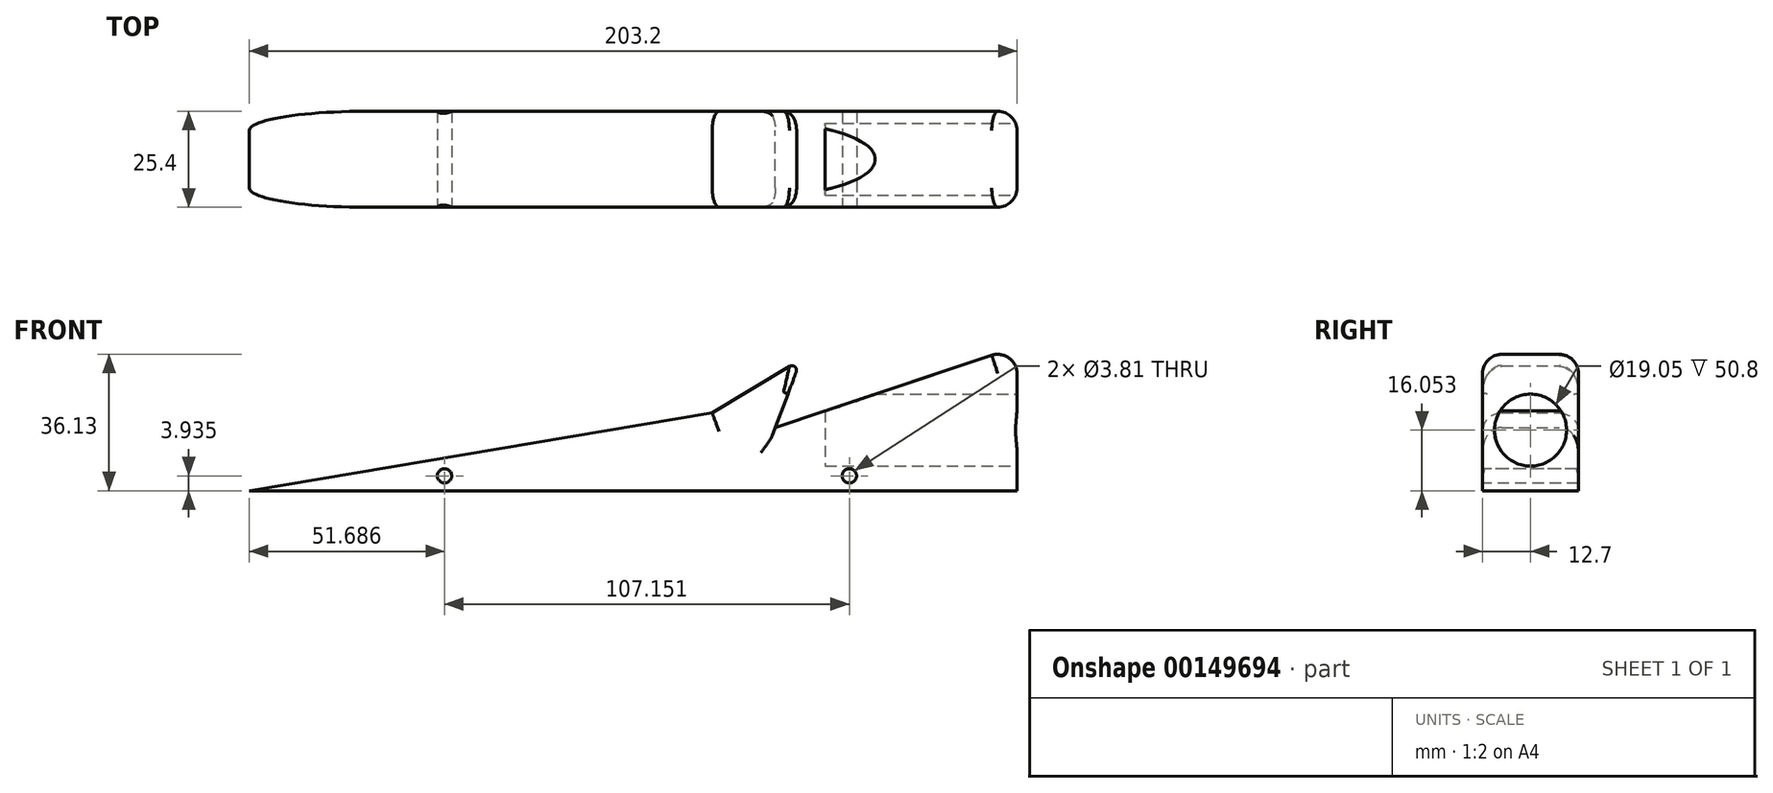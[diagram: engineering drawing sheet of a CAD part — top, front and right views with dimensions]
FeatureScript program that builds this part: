
annotation { "Feature Type Name" : "Feature", "Feature Type Description" : "" }
export const myFeature = defineFeature(function(context is Context, id is Id, definition is map)
    precondition{}
    {
        {
            var Q0;
            Q0=qCreatedBy(makeId("Front.planeOp"),FACE);
            var sketch = newSketch(context, id + "F0", { "sketchPlane" : qUnion([Q0])});
            skLineSegment(sketch, "E0", {"start": v(-98.76, 0) * mm, "end": v(104.44, 0) * mm});
            skLineSegment(sketch, "E1", {"start": v(104.44, 0) * mm, "end": v(104.44, 38.1) * mm});
            skLineSegment(sketch, "E2", {"start": v(-98.76, 0) * mm, "end": v(23.78, 20.59) * mm});
            skLineSegment(sketch, "E3", {"start": v(23.78, 20.59) * mm, "end": v(47.26, 34.81) * mm});
            skLineSegment(sketch, "E4", {"start": v(47.26, 34.81) * mm, "end": v(40.49, 16.75) * mm});
            skLineSegment(sketch, "E5", {"start": v(40.49, 16.75) * mm, "end": v(104.44, 38.1) * mm});
            skSolve(sketch);
        }
        {
            var Q0;
            Q0 = qSketchRegion(id + "F0", true);
            extrude(context, id + "F1", {"entities" : qUnion([Q0]), "depth" : 25.4 * mm});
        }
        {
            var Q0;
            Q0=makeQuery(id+"F1.opExtrude","SWEPT_FACE",FACE,{"disambiguationData":[OSD([sQuery(id+"F0.wireOp",EDGE,"E1")])]});
            var sketch = newSketch(context, id + "F2", { "sketchPlane" : qUnion([Q0])});
            skCircle(sketch, "E6", {"center": v(-12.7, 16.05) * mm, "radius": 9.53 * mm});
            skSolve(sketch);
        }
        {
            var Q0;
            Q0=makeQuery(id+"F1.opExtrude","CAP_FACE",FACE,{"disambiguationData":[OSD([sQuery(id+"F0.wireOp",EDGE,"E0"),sQuery(id+"F0.wireOp",EDGE,"E1"),sQuery(id+"F0.wireOp",EDGE,"E2"),sQuery(id+"F0.wireOp",EDGE,"E3"),sQuery(id+"F0.wireOp",EDGE,"E4"),sQuery(id+"F0.wireOp",EDGE,"E5")])],"isStart":false});
            var sketch = newSketch(context, id + "F3", { "sketchPlane" : qUnion([Q0])});
            skCircle(sketch, "E7", {"center": v(-47.07, 3.93) * mm, "radius": 1.9 * mm});
            skCircle(sketch, "E8", {"center": v(60.08, 3.93) * mm, "radius": 1.9 * mm});
            skSolve(sketch);
        }
        {
            var Q0;
            Q0 = qSketchRegion(id + "F3", true);
            extrude(context, id + "F4", {"entities" : qUnion([Q0]), "operationType" : NewBodyOperationType.REMOVE, "oppositeDirection" : true, "depth" : 25.4 * mm});
        }
        {
            var Q0;
            Q0 = qSketchRegion(id + "F2", true);
            extrude(context, id + "F5", {"entities" : qUnion([Q0]), "operationType" : NewBodyOperationType.REMOVE, "oppositeDirection" : true, "depth" : 50.8 * mm});
        }
        {
            var Q0;
            Q0=makeQuery(id+"F1.opExtrude","CAP_EDGE",EDGE,{"disambiguationData":[OSD([sQuery(id+"F0.wireOp",EDGE,"E2")])],"isStart":false});
            var Q1;
            Q1=makeQuery(id+"F1.opExtrude","CAP_EDGE",EDGE,{"disambiguationData":[OSD([sQuery(id+"F0.wireOp",EDGE,"E2")])],"isStart":true});
            var Q2;
            Q2=makeQuery(id+"F1.opExtrude","CAP_EDGE",EDGE,{"disambiguationData":[OSD([sQuery(id+"F0.wireOp",EDGE,"E3")])],"isStart":true});
            var Q3;
            Q3=makeQuery(id+"F1.opExtrude","CAP_EDGE",EDGE,{"disambiguationData":[OSD([sQuery(id+"F0.wireOp",EDGE,"E3")])],"isStart":false});
            fillet(context, id + "F6", {"entities" : qUnion([Q0, Q1, Q2, Q3]), "radius" : 5.08 * mm, "tangentPropagation" : true, "allowEdgeOverflow" : false});
        }
        {
            var Q0;
            Q0=makeQuery(id+"F1.opExtrude","CAP_EDGE",EDGE,{"disambiguationData":[OSD([sQuery(id+"F0.wireOp",EDGE,"E5")])],"isStart":false});
            var Q1;
            Q1=makeQuery(id+"F1.opExtrude","CAP_EDGE",EDGE,{"disambiguationData":[OSD([sQuery(id+"F0.wireOp",EDGE,"E5")])],"isStart":true});
            fillet(context, id + "F7", {"entities" : qUnion([Q0, Q1]), "radius" : 5.08 * mm, "tangentPropagation" : true, "allowEdgeOverflow" : false});
        }
        {
            var Q0;
            Q0=makeQuery(id+"F1.opExtrude","SWEPT_EDGE",EDGE,{"disambiguationData":[OSD([sQuery(id+"F0.wireOp",EDGE,"E3"),sQuery(id+"F0.wireOp",EDGE,"E4")])]});
            fillet(context, id + "F8", {"entities" : qUnion([Q0]), "radius" : 1.24 * mm, "tangentPropagation" : true, "allowEdgeOverflow" : false});
        }
        {
            var Q0;
            Q0=makeQuery(id+"F7.opFillet","BLEND_EDGE",EDGE,{"blendedFrom":[makeQuery(id+"F1.opExtrude","CAP_EDGE",EDGE,{"disambiguationData":[OSD([sQuery(id+"F0.wireOp",EDGE,"E5")])],"isStart":false}),makeQuery(id+"F1.opExtrude","SWEPT_FACE",FACE,{"disambiguationData":[OSD([sQuery(id+"F0.wireOp",EDGE,"E1")])]})],"blendedInto":[makeQuery(id+"F1.opExtrude","SWEPT_FACE",FACE,{"disambiguationData":[OSD([sQuery(id+"F0.wireOp",EDGE,"E1")])]})]});
            var Q1;
            Q1=makeQuery(id+"F1.opExtrude","SWEPT_EDGE",EDGE,{"disambiguationData":[OSD([sQuery(id+"F0.wireOp",EDGE,"E1"),sQuery(id+"F0.wireOp",EDGE,"E5")])]});
            var Q2;
            Q2=makeQuery(id+"F7.opFillet","BLEND_EDGE",EDGE,{"blendedFrom":[makeQuery(id+"F1.opExtrude","CAP_EDGE",EDGE,{"disambiguationData":[OSD([sQuery(id+"F0.wireOp",EDGE,"E5")])],"isStart":true}),makeQuery(id+"F1.opExtrude","SWEPT_FACE",FACE,{"disambiguationData":[OSD([sQuery(id+"F0.wireOp",EDGE,"E1")])]})],"blendedInto":[makeQuery(id+"F1.opExtrude","SWEPT_FACE",FACE,{"disambiguationData":[OSD([sQuery(id+"F0.wireOp",EDGE,"E1")])]})]});
            fillet(context, id + "F9", {"entities" : qUnion([Q0, Q1, Q2]), "radius" : 5.08 * mm, "tangentPropagation" : true, "allowEdgeOverflow" : false});
        }
    });
